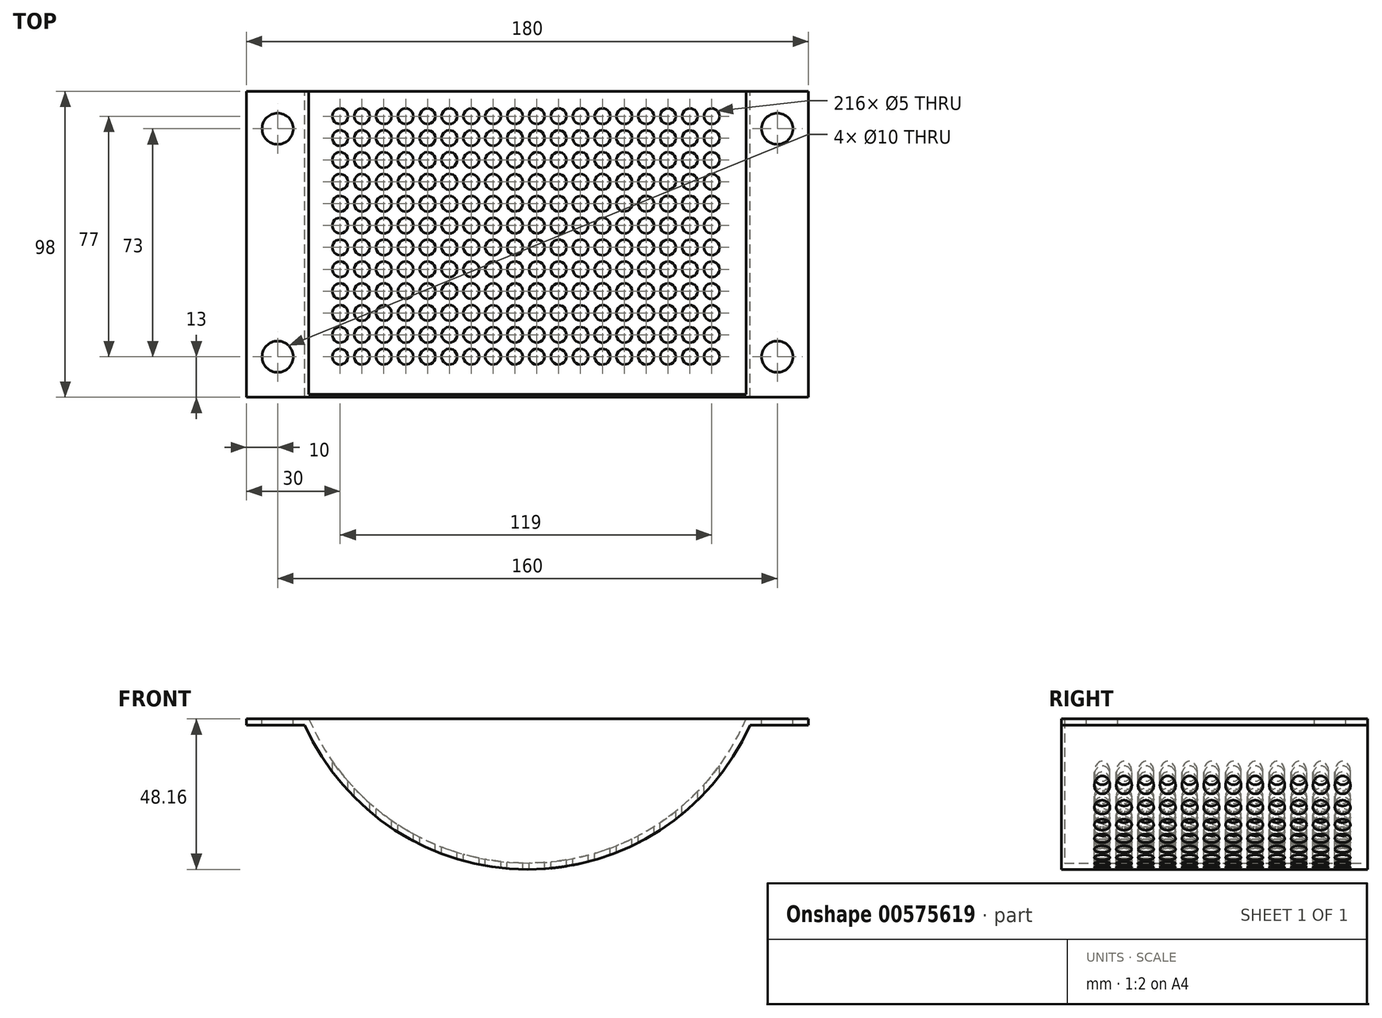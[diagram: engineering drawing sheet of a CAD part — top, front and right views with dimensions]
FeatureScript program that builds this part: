
annotation { "Feature Type Name" : "Feature", "Feature Type Description" : "" }
export const myFeature = defineFeature(function(context is Context, id is Id, definition is map)
    precondition{}
    {
        {
            var Q0;
            Q0=qCreatedBy(makeId("Front.planeOp"),FACE);
            var sketch = newSketch(context, id + "F0", { "sketchPlane" : qUnion([Q0])});
            skArc(sketch, "E0", {"start": v(-70, 0) * mm, "mid": v(-41.92, -33.58) * mm, "end": v(0, -46.16) * mm});
            skLineSegment(sketch, "E1", {"start": v(-70, 0) * mm, "end": v(-90, 0) * mm});
            skLineSegment(sketch, "E2", {"start": v(0, 0) * mm, "end": v(0, -46.16) * mm});
            skLineSegment(sketch, "E3.0", {"start": v(-71.3, -2) * mm, "end": v(-90, -2) * mm});
            skArc(sketch, "E3.1", {"start": v(-71.3, -2) * mm, "mid": v(-42.47, -35.61) * mm, "end": v(0, -48.16) * mm});
            skLineSegment(sketch, "E4", {"start": v(-90, 0) * mm, "end": v(-90, -2) * mm});
            skArc(sketch, "E5.MirrorCS", {"start": v(70, 0) * mm, "mid": v(41.92, -33.58) * mm, "end": v(0, -46.16) * mm});
            skArc(sketch, "E6.MirrorCS", {"start": v(71.3, -2) * mm, "mid": v(42.47, -35.61) * mm, "end": v(0, -48.16) * mm});
            skLineSegment(sketch, "E7.MirrorCS", {"start": v(71.3, -2) * mm, "end": v(90, -2) * mm});
            skLineSegment(sketch, "E8.MirrorCS", {"start": v(70, 0) * mm, "end": v(90, 0) * mm});
            skLineSegment(sketch, "E9.MirrorCS", {"start": v(90, 0) * mm, "end": v(90, -2) * mm});
            skSolve(sketch);
        }
        {
            var Q0;
            Q0 = qSketchRegion(id + "F0", true);
            extrude(context, id + "F1", {"entities" : qUnion([Q0]), "depth" : 97 * mm, "offsetDistance" : 25 * mm});
        }
        {
            var Q0;
            Q0=qCreatedBy(makeId("Top.planeOp"),FACE);
            var sketch = newSketch(context, id + "F2", { "sketchPlane" : qUnion([Q0])});
            skCircle(sketch, "E10", {"center": v(-60, -8) * mm, "radius": 2.5 * mm});
            skCircle(sketch, "E11.1.0.0", {"center": v(-53, -8) * mm, "radius": 2.5 * mm});
            skCircle(sketch, "E11.2.0.0", {"center": v(-46, -8) * mm, "radius": 2.5 * mm});
            skCircle(sketch, "E11.3.0.0", {"center": v(-39, -8) * mm, "radius": 2.5 * mm});
            skCircle(sketch, "E11.4.0.0", {"center": v(-32, -8) * mm, "radius": 2.5 * mm});
            skCircle(sketch, "E11.5.0.0", {"center": v(-25, -8) * mm, "radius": 2.5 * mm});
            skCircle(sketch, "E11.6.0.0", {"center": v(-18, -8) * mm, "radius": 2.5 * mm});
            skCircle(sketch, "E11.7.0.0", {"center": v(-11, -8) * mm, "radius": 2.5 * mm});
            skCircle(sketch, "E11.8.0.0", {"center": v(-4, -8) * mm, "radius": 2.5 * mm});
            skCircle(sketch, "E11.9.0.0", {"center": v(3, -8) * mm, "radius": 2.5 * mm});
            skCircle(sketch, "E11.10.0.0", {"center": v(10, -8) * mm, "radius": 2.5 * mm});
            skCircle(sketch, "E11.11.0.0", {"center": v(17, -8) * mm, "radius": 2.5 * mm});
            skCircle(sketch, "E11.12.0.0", {"center": v(24, -8) * mm, "radius": 2.5 * mm});
            skCircle(sketch, "E11.13.0.0", {"center": v(31, -8) * mm, "radius": 2.5 * mm});
            skCircle(sketch, "E11.14.0.0", {"center": v(38, -8) * mm, "radius": 2.5 * mm});
            skCircle(sketch, "E11.15.0.0", {"center": v(45, -8) * mm, "radius": 2.5 * mm});
            skCircle(sketch, "E11.16.0.0", {"center": v(52, -8) * mm, "radius": 2.5 * mm});
            skCircle(sketch, "E11.17.0.0", {"center": v(59, -8) * mm, "radius": 2.5 * mm});
            skLineSegment(sketch, "E11.direction1", {"start": v(-60, -8) * mm, "end": v(-53, -8) * mm, "construction": true});
            skCircle(sketch, "E12.1.0.0", {"center": v(-60, -15) * mm, "radius": 2.5 * mm});
            skCircle(sketch, "E12.1.0.1", {"center": v(-53, -15) * mm, "radius": 2.5 * mm});
            skCircle(sketch, "E12.1.0.2", {"center": v(-46, -15) * mm, "radius": 2.5 * mm});
            skCircle(sketch, "E12.1.0.3", {"center": v(-39, -15) * mm, "radius": 2.5 * mm});
            skCircle(sketch, "E12.1.0.4", {"center": v(-32, -15) * mm, "radius": 2.5 * mm});
            skCircle(sketch, "E12.1.0.5", {"center": v(-25, -15) * mm, "radius": 2.5 * mm});
            skCircle(sketch, "E12.1.0.6", {"center": v(-18, -15) * mm, "radius": 2.5 * mm});
            skCircle(sketch, "E12.1.0.7", {"center": v(-11, -15) * mm, "radius": 2.5 * mm});
            skCircle(sketch, "E12.1.0.8", {"center": v(-4, -15) * mm, "radius": 2.5 * mm});
            skCircle(sketch, "E12.1.0.9", {"center": v(3, -15) * mm, "radius": 2.5 * mm});
            skCircle(sketch, "E12.1.0.10", {"center": v(10, -15) * mm, "radius": 2.5 * mm});
            skCircle(sketch, "E12.1.0.11", {"center": v(17, -15) * mm, "radius": 2.5 * mm});
            skCircle(sketch, "E12.1.0.12", {"center": v(31, -15) * mm, "radius": 2.5 * mm});
            skCircle(sketch, "E12.1.0.13", {"center": v(38, -15) * mm, "radius": 2.5 * mm});
            skCircle(sketch, "E12.1.0.14", {"center": v(45, -15) * mm, "radius": 2.5 * mm});
            skCircle(sketch, "E12.1.0.15", {"center": v(52, -15) * mm, "radius": 2.5 * mm});
            skCircle(sketch, "E12.1.0.16", {"center": v(59, -15) * mm, "radius": 2.5 * mm});
            skCircle(sketch, "E12.2.0.0", {"center": v(-60, -22) * mm, "radius": 2.5 * mm});
            skCircle(sketch, "E12.2.0.1", {"center": v(-53, -22) * mm, "radius": 2.5 * mm});
            skCircle(sketch, "E12.2.0.2", {"center": v(-46, -22) * mm, "radius": 2.5 * mm});
            skCircle(sketch, "E12.2.0.3", {"center": v(-39, -22) * mm, "radius": 2.5 * mm});
            skCircle(sketch, "E12.2.0.4", {"center": v(-32, -22) * mm, "radius": 2.5 * mm});
            skCircle(sketch, "E12.2.0.5", {"center": v(-25, -22) * mm, "radius": 2.5 * mm});
            skCircle(sketch, "E12.2.0.6", {"center": v(-18, -22) * mm, "radius": 2.5 * mm});
            skCircle(sketch, "E12.2.0.7", {"center": v(-11, -22) * mm, "radius": 2.5 * mm});
            skCircle(sketch, "E12.2.0.8", {"center": v(-4, -22) * mm, "radius": 2.5 * mm});
            skCircle(sketch, "E12.2.0.9", {"center": v(3, -22) * mm, "radius": 2.5 * mm});
            skCircle(sketch, "E12.2.0.10", {"center": v(10, -22) * mm, "radius": 2.5 * mm});
            skCircle(sketch, "E12.2.0.11", {"center": v(17, -22) * mm, "radius": 2.5 * mm});
            skCircle(sketch, "E12.2.0.12", {"center": v(31, -22) * mm, "radius": 2.5 * mm});
            skCircle(sketch, "E12.2.0.13", {"center": v(38, -22) * mm, "radius": 2.5 * mm});
            skCircle(sketch, "E12.2.0.14", {"center": v(45, -22) * mm, "radius": 2.5 * mm});
            skCircle(sketch, "E12.2.0.15", {"center": v(52, -22) * mm, "radius": 2.5 * mm});
            skCircle(sketch, "E12.2.0.16", {"center": v(59, -22) * mm, "radius": 2.5 * mm});
            skCircle(sketch, "E12.3.0.0", {"center": v(-60, -29) * mm, "radius": 2.5 * mm});
            skCircle(sketch, "E12.3.0.1", {"center": v(-53, -29) * mm, "radius": 2.5 * mm});
            skCircle(sketch, "E12.3.0.2", {"center": v(-46, -29) * mm, "radius": 2.5 * mm});
            skCircle(sketch, "E12.3.0.3", {"center": v(-39, -29) * mm, "radius": 2.5 * mm});
            skCircle(sketch, "E12.3.0.4", {"center": v(-32, -29) * mm, "radius": 2.5 * mm});
            skCircle(sketch, "E12.3.0.5", {"center": v(-25, -29) * mm, "radius": 2.5 * mm});
            skCircle(sketch, "E12.3.0.6", {"center": v(-18, -29) * mm, "radius": 2.5 * mm});
            skCircle(sketch, "E12.3.0.7", {"center": v(-11, -29) * mm, "radius": 2.5 * mm});
            skCircle(sketch, "E12.3.0.8", {"center": v(-4, -29) * mm, "radius": 2.5 * mm});
            skCircle(sketch, "E12.3.0.9", {"center": v(3, -29) * mm, "radius": 2.5 * mm});
            skCircle(sketch, "E12.3.0.10", {"center": v(10, -29) * mm, "radius": 2.5 * mm});
            skCircle(sketch, "E12.3.0.11", {"center": v(17, -29) * mm, "radius": 2.5 * mm});
            skCircle(sketch, "E12.3.0.12", {"center": v(31, -29) * mm, "radius": 2.5 * mm});
            skCircle(sketch, "E12.3.0.13", {"center": v(38, -29) * mm, "radius": 2.5 * mm});
            skCircle(sketch, "E12.3.0.14", {"center": v(45, -29) * mm, "radius": 2.5 * mm});
            skCircle(sketch, "E12.3.0.15", {"center": v(52, -29) * mm, "radius": 2.5 * mm});
            skCircle(sketch, "E12.3.0.16", {"center": v(59, -29) * mm, "radius": 2.5 * mm});
            skCircle(sketch, "E12.4.0.0", {"center": v(-60, -36) * mm, "radius": 2.5 * mm});
            skCircle(sketch, "E12.4.0.1", {"center": v(-53, -36) * mm, "radius": 2.5 * mm});
            skCircle(sketch, "E12.4.0.2", {"center": v(-46, -36) * mm, "radius": 2.5 * mm});
            skCircle(sketch, "E12.4.0.3", {"center": v(-39, -36) * mm, "radius": 2.5 * mm});
            skCircle(sketch, "E12.4.0.4", {"center": v(-32, -36) * mm, "radius": 2.5 * mm});
            skCircle(sketch, "E12.4.0.5", {"center": v(-25, -36) * mm, "radius": 2.5 * mm});
            skCircle(sketch, "E12.4.0.6", {"center": v(-18, -36) * mm, "radius": 2.5 * mm});
            skCircle(sketch, "E12.4.0.7", {"center": v(-11, -36) * mm, "radius": 2.5 * mm});
            skCircle(sketch, "E12.4.0.8", {"center": v(-4, -36) * mm, "radius": 2.5 * mm});
            skCircle(sketch, "E12.4.0.9", {"center": v(3, -36) * mm, "radius": 2.5 * mm});
            skCircle(sketch, "E12.4.0.10", {"center": v(10, -36) * mm, "radius": 2.5 * mm});
            skCircle(sketch, "E12.4.0.11", {"center": v(17, -36) * mm, "radius": 2.5 * mm});
            skCircle(sketch, "E12.4.0.12", {"center": v(31, -36) * mm, "radius": 2.5 * mm});
            skCircle(sketch, "E12.4.0.13", {"center": v(38, -36) * mm, "radius": 2.5 * mm});
            skCircle(sketch, "E12.4.0.14", {"center": v(45, -36) * mm, "radius": 2.5 * mm});
            skCircle(sketch, "E12.4.0.15", {"center": v(52, -36) * mm, "radius": 2.5 * mm});
            skCircle(sketch, "E12.4.0.16", {"center": v(59, -36) * mm, "radius": 2.5 * mm});
            skCircle(sketch, "E12.5.0.0", {"center": v(-60, -43) * mm, "radius": 2.5 * mm});
            skCircle(sketch, "E12.5.0.1", {"center": v(-53, -43) * mm, "radius": 2.5 * mm});
            skCircle(sketch, "E12.5.0.2", {"center": v(-46, -43) * mm, "radius": 2.5 * mm});
            skCircle(sketch, "E12.5.0.3", {"center": v(-39, -43) * mm, "radius": 2.5 * mm});
            skCircle(sketch, "E12.5.0.4", {"center": v(-32, -43) * mm, "radius": 2.5 * mm});
            skCircle(sketch, "E12.5.0.5", {"center": v(-25, -43) * mm, "radius": 2.5 * mm});
            skCircle(sketch, "E12.5.0.6", {"center": v(-18, -43) * mm, "radius": 2.5 * mm});
            skCircle(sketch, "E12.5.0.7", {"center": v(-11, -43) * mm, "radius": 2.5 * mm});
            skCircle(sketch, "E12.5.0.8", {"center": v(-4, -43) * mm, "radius": 2.5 * mm});
            skCircle(sketch, "E12.5.0.9", {"center": v(3, -43) * mm, "radius": 2.5 * mm});
            skCircle(sketch, "E12.5.0.10", {"center": v(10, -43) * mm, "radius": 2.5 * mm});
            skCircle(sketch, "E12.5.0.11", {"center": v(17, -43) * mm, "radius": 2.5 * mm});
            skCircle(sketch, "E12.5.0.12", {"center": v(31, -43) * mm, "radius": 2.5 * mm});
            skCircle(sketch, "E12.5.0.13", {"center": v(38, -43) * mm, "radius": 2.5 * mm});
            skCircle(sketch, "E12.5.0.14", {"center": v(45, -43) * mm, "radius": 2.5 * mm});
            skCircle(sketch, "E12.5.0.15", {"center": v(52, -43) * mm, "radius": 2.5 * mm});
            skCircle(sketch, "E12.5.0.16", {"center": v(59, -43) * mm, "radius": 2.5 * mm});
            skCircle(sketch, "E12.6.0.0", {"center": v(-60, -50) * mm, "radius": 2.5 * mm});
            skCircle(sketch, "E12.6.0.1", {"center": v(-53, -50) * mm, "radius": 2.5 * mm});
            skCircle(sketch, "E12.6.0.2", {"center": v(-46, -50) * mm, "radius": 2.5 * mm});
            skCircle(sketch, "E12.6.0.3", {"center": v(-39, -50) * mm, "radius": 2.5 * mm});
            skCircle(sketch, "E12.6.0.4", {"center": v(-32, -50) * mm, "radius": 2.5 * mm});
            skCircle(sketch, "E12.6.0.5", {"center": v(-25, -50) * mm, "radius": 2.5 * mm});
            skCircle(sketch, "E12.6.0.6", {"center": v(-18, -50) * mm, "radius": 2.5 * mm});
            skCircle(sketch, "E12.6.0.7", {"center": v(-11, -50) * mm, "radius": 2.5 * mm});
            skCircle(sketch, "E12.6.0.8", {"center": v(-4, -50) * mm, "radius": 2.5 * mm});
            skCircle(sketch, "E12.6.0.9", {"center": v(3, -50) * mm, "radius": 2.5 * mm});
            skCircle(sketch, "E12.6.0.10", {"center": v(10, -50) * mm, "radius": 2.5 * mm});
            skCircle(sketch, "E12.6.0.11", {"center": v(17, -50) * mm, "radius": 2.5 * mm});
            skCircle(sketch, "E12.6.0.12", {"center": v(31, -50) * mm, "radius": 2.5 * mm});
            skCircle(sketch, "E12.6.0.13", {"center": v(38, -50) * mm, "radius": 2.5 * mm});
            skCircle(sketch, "E12.6.0.14", {"center": v(45, -50) * mm, "radius": 2.5 * mm});
            skCircle(sketch, "E12.6.0.15", {"center": v(52, -50) * mm, "radius": 2.5 * mm});
            skCircle(sketch, "E12.6.0.16", {"center": v(59, -50) * mm, "radius": 2.5 * mm});
            skCircle(sketch, "E12.7.0.0", {"center": v(-60, -57) * mm, "radius": 2.5 * mm});
            skCircle(sketch, "E12.7.0.1", {"center": v(-53, -57) * mm, "radius": 2.5 * mm});
            skCircle(sketch, "E12.7.0.2", {"center": v(-46, -57) * mm, "radius": 2.5 * mm});
            skCircle(sketch, "E12.7.0.3", {"center": v(-39, -57) * mm, "radius": 2.5 * mm});
            skCircle(sketch, "E12.7.0.4", {"center": v(-32, -57) * mm, "radius": 2.5 * mm});
            skCircle(sketch, "E12.7.0.5", {"center": v(-25, -57) * mm, "radius": 2.5 * mm});
            skCircle(sketch, "E12.7.0.6", {"center": v(-18, -57) * mm, "radius": 2.5 * mm});
            skCircle(sketch, "E12.7.0.7", {"center": v(-11, -57) * mm, "radius": 2.5 * mm});
            skCircle(sketch, "E12.7.0.8", {"center": v(-4, -57) * mm, "radius": 2.5 * mm});
            skCircle(sketch, "E12.7.0.9", {"center": v(3, -57) * mm, "radius": 2.5 * mm});
            skCircle(sketch, "E12.7.0.10", {"center": v(10, -57) * mm, "radius": 2.5 * mm});
            skCircle(sketch, "E12.7.0.11", {"center": v(17, -57) * mm, "radius": 2.5 * mm});
            skCircle(sketch, "E12.7.0.12", {"center": v(31, -57) * mm, "radius": 2.5 * mm});
            skCircle(sketch, "E12.7.0.13", {"center": v(38, -57) * mm, "radius": 2.5 * mm});
            skCircle(sketch, "E12.7.0.14", {"center": v(45, -57) * mm, "radius": 2.5 * mm});
            skCircle(sketch, "E12.7.0.15", {"center": v(52, -57) * mm, "radius": 2.5 * mm});
            skCircle(sketch, "E12.7.0.16", {"center": v(59, -57) * mm, "radius": 2.5 * mm});
            skCircle(sketch, "E12.8.0.0", {"center": v(-60, -64) * mm, "radius": 2.5 * mm});
            skCircle(sketch, "E12.8.0.1", {"center": v(-53, -64) * mm, "radius": 2.5 * mm});
            skCircle(sketch, "E12.8.0.2", {"center": v(-46, -64) * mm, "radius": 2.5 * mm});
            skCircle(sketch, "E12.8.0.3", {"center": v(-39, -64) * mm, "radius": 2.5 * mm});
            skCircle(sketch, "E12.8.0.4", {"center": v(-32, -64) * mm, "radius": 2.5 * mm});
            skCircle(sketch, "E12.8.0.5", {"center": v(-25, -64) * mm, "radius": 2.5 * mm});
            skCircle(sketch, "E12.8.0.6", {"center": v(-18, -64) * mm, "radius": 2.5 * mm});
            skCircle(sketch, "E12.8.0.7", {"center": v(-11, -64) * mm, "radius": 2.5 * mm});
            skCircle(sketch, "E12.8.0.8", {"center": v(-4, -64) * mm, "radius": 2.5 * mm});
            skCircle(sketch, "E12.8.0.9", {"center": v(3, -64) * mm, "radius": 2.5 * mm});
            skCircle(sketch, "E12.8.0.10", {"center": v(10, -64) * mm, "radius": 2.5 * mm});
            skCircle(sketch, "E12.8.0.11", {"center": v(17, -64) * mm, "radius": 2.5 * mm});
            skCircle(sketch, "E12.8.0.12", {"center": v(31, -64) * mm, "radius": 2.5 * mm});
            skCircle(sketch, "E12.8.0.13", {"center": v(38, -64) * mm, "radius": 2.5 * mm});
            skCircle(sketch, "E12.8.0.14", {"center": v(45, -64) * mm, "radius": 2.5 * mm});
            skCircle(sketch, "E12.8.0.15", {"center": v(52, -64) * mm, "radius": 2.5 * mm});
            skCircle(sketch, "E12.8.0.16", {"center": v(59, -64) * mm, "radius": 2.5 * mm});
            skCircle(sketch, "E12.9.0.0", {"center": v(-60, -71) * mm, "radius": 2.5 * mm});
            skCircle(sketch, "E12.9.0.1", {"center": v(-53, -71) * mm, "radius": 2.5 * mm});
            skCircle(sketch, "E12.9.0.2", {"center": v(-46, -71) * mm, "radius": 2.5 * mm});
            skCircle(sketch, "E12.9.0.3", {"center": v(-39, -71) * mm, "radius": 2.5 * mm});
            skCircle(sketch, "E12.9.0.4", {"center": v(-32, -71) * mm, "radius": 2.5 * mm});
            skCircle(sketch, "E12.9.0.5", {"center": v(-25, -71) * mm, "radius": 2.5 * mm});
            skCircle(sketch, "E12.9.0.6", {"center": v(-18, -71) * mm, "radius": 2.5 * mm});
            skCircle(sketch, "E12.9.0.7", {"center": v(-11, -71) * mm, "radius": 2.5 * mm});
            skCircle(sketch, "E12.9.0.8", {"center": v(-4, -71) * mm, "radius": 2.5 * mm});
            skCircle(sketch, "E12.9.0.9", {"center": v(3, -71) * mm, "radius": 2.5 * mm});
            skCircle(sketch, "E12.9.0.10", {"center": v(10, -71) * mm, "radius": 2.5 * mm});
            skCircle(sketch, "E12.9.0.11", {"center": v(17, -71) * mm, "radius": 2.5 * mm});
            skCircle(sketch, "E12.9.0.12", {"center": v(31, -71) * mm, "radius": 2.5 * mm});
            skCircle(sketch, "E12.9.0.13", {"center": v(38, -71) * mm, "radius": 2.5 * mm});
            skCircle(sketch, "E12.9.0.14", {"center": v(45, -71) * mm, "radius": 2.5 * mm});
            skCircle(sketch, "E12.9.0.15", {"center": v(52, -71) * mm, "radius": 2.5 * mm});
            skCircle(sketch, "E12.9.0.16", {"center": v(59, -71) * mm, "radius": 2.5 * mm});
            skCircle(sketch, "E12.10.0.0", {"center": v(-60, -78) * mm, "radius": 2.5 * mm});
            skCircle(sketch, "E12.10.0.1", {"center": v(-53, -78) * mm, "radius": 2.5 * mm});
            skCircle(sketch, "E12.10.0.2", {"center": v(-46, -78) * mm, "radius": 2.5 * mm});
            skCircle(sketch, "E12.10.0.3", {"center": v(-39, -78) * mm, "radius": 2.5 * mm});
            skCircle(sketch, "E12.10.0.4", {"center": v(-32, -78) * mm, "radius": 2.5 * mm});
            skCircle(sketch, "E12.10.0.5", {"center": v(-25, -78) * mm, "radius": 2.5 * mm});
            skCircle(sketch, "E12.10.0.6", {"center": v(-18, -78) * mm, "radius": 2.5 * mm});
            skCircle(sketch, "E12.10.0.7", {"center": v(-11, -78) * mm, "radius": 2.5 * mm});
            skCircle(sketch, "E12.10.0.8", {"center": v(-4, -78) * mm, "radius": 2.5 * mm});
            skCircle(sketch, "E12.10.0.9", {"center": v(3, -78) * mm, "radius": 2.5 * mm});
            skCircle(sketch, "E12.10.0.10", {"center": v(10, -78) * mm, "radius": 2.5 * mm});
            skCircle(sketch, "E12.10.0.11", {"center": v(17, -78) * mm, "radius": 2.5 * mm});
            skCircle(sketch, "E12.10.0.12", {"center": v(31, -78) * mm, "radius": 2.5 * mm});
            skCircle(sketch, "E12.10.0.13", {"center": v(38, -78) * mm, "radius": 2.5 * mm});
            skCircle(sketch, "E12.10.0.14", {"center": v(45, -78) * mm, "radius": 2.5 * mm});
            skCircle(sketch, "E12.10.0.15", {"center": v(52, -78) * mm, "radius": 2.5 * mm});
            skCircle(sketch, "E12.10.0.16", {"center": v(59, -78) * mm, "radius": 2.5 * mm});
            skCircle(sketch, "E12.11.0.0", {"center": v(-60, -85) * mm, "radius": 2.5 * mm});
            skCircle(sketch, "E12.11.0.1", {"center": v(-53, -85) * mm, "radius": 2.5 * mm});
            skCircle(sketch, "E12.11.0.2", {"center": v(-46, -85) * mm, "radius": 2.5 * mm});
            skCircle(sketch, "E12.11.0.3", {"center": v(-39, -85) * mm, "radius": 2.5 * mm});
            skCircle(sketch, "E12.11.0.4", {"center": v(-32, -85) * mm, "radius": 2.5 * mm});
            skCircle(sketch, "E12.11.0.5", {"center": v(-25, -85) * mm, "radius": 2.5 * mm});
            skCircle(sketch, "E12.11.0.6", {"center": v(-18, -85) * mm, "radius": 2.5 * mm});
            skCircle(sketch, "E12.11.0.7", {"center": v(-11, -85) * mm, "radius": 2.5 * mm});
            skCircle(sketch, "E12.11.0.8", {"center": v(-4, -85) * mm, "radius": 2.5 * mm});
            skCircle(sketch, "E12.11.0.9", {"center": v(3, -85) * mm, "radius": 2.5 * mm});
            skCircle(sketch, "E12.11.0.10", {"center": v(10, -85) * mm, "radius": 2.5 * mm});
            skCircle(sketch, "E12.11.0.11", {"center": v(17, -85) * mm, "radius": 2.5 * mm});
            skCircle(sketch, "E12.11.0.12", {"center": v(31, -85) * mm, "radius": 2.5 * mm});
            skCircle(sketch, "E12.11.0.13", {"center": v(38, -85) * mm, "radius": 2.5 * mm});
            skCircle(sketch, "E12.11.0.14", {"center": v(45, -85) * mm, "radius": 2.5 * mm});
            skCircle(sketch, "E12.11.0.15", {"center": v(52, -85) * mm, "radius": 2.5 * mm});
            skCircle(sketch, "E12.11.0.16", {"center": v(59, -85) * mm, "radius": 2.5 * mm});
            skLineSegment(sketch, "E12.direction1", {"start": v(-60, -8) * mm, "end": v(-60, -15) * mm, "construction": true});
            skCircle(sketch, "E13.1.0.0", {"center": v(24, -15) * mm, "radius": 2.5 * mm});
            skCircle(sketch, "E13.2.0.0", {"center": v(24, -22) * mm, "radius": 2.5 * mm});
            skCircle(sketch, "E13.3.0.0", {"center": v(24, -29) * mm, "radius": 2.5 * mm});
            skCircle(sketch, "E13.4.0.0", {"center": v(24, -36) * mm, "radius": 2.5 * mm});
            skCircle(sketch, "E13.5.0.0", {"center": v(24, -43) * mm, "radius": 2.5 * mm});
            skCircle(sketch, "E13.6.0.0", {"center": v(24, -50) * mm, "radius": 2.5 * mm});
            skCircle(sketch, "E13.7.0.0", {"center": v(24, -57) * mm, "radius": 2.5 * mm});
            skCircle(sketch, "E13.8.0.0", {"center": v(24, -64) * mm, "radius": 2.5 * mm});
            skCircle(sketch, "E13.9.0.0", {"center": v(24, -71) * mm, "radius": 2.5 * mm});
            skCircle(sketch, "E13.10.0.0", {"center": v(24, -78) * mm, "radius": 2.5 * mm});
            skCircle(sketch, "E13.11.0.0", {"center": v(24, -85) * mm, "radius": 2.5 * mm});
            skLineSegment(sketch, "E13.direction1", {"start": v(24, -8) * mm, "end": v(24, -15) * mm, "construction": true});
            skSolve(sketch);
        }
        {
            var Q0;
            Q0 = qSketchRegion(id + "F2", true);
            extrude(context, id + "F3", {"entities" : qUnion([Q0]), "operationType" : NewBodyOperationType.REMOVE, "endBound" : BoundingType.THROUGH_ALL, "oppositeDirection" : true, "depth" : 25 * mm, "offsetDistance" : 25 * mm});
        }
        {
            var Q0;
            Q0=qCreatedBy(makeId("Top.planeOp"),FACE);
            var sketch = newSketch(context, id + "F4", { "sketchPlane" : qUnion([Q0])});
            skCircle(sketch, "E14", {"center": v(-80, -12) * mm, "radius": 5 * mm});
            skCircle(sketch, "E15.MirrorC", {"center": v(80, -12) * mm, "radius": 5 * mm});
            skLineSegment(sketch, "E16", {"start": v(90.51, -48.5) * mm, "end": v(-112.77, -48.5) * mm});
            skLineSegment(sketch, "E17", {"start": v(0, 0) * mm, "end": v(0, -97) * mm});
            skCircle(sketch, "E18.MirrorC", {"center": v(-80, -85) * mm, "radius": 5 * mm});
            skCircle(sketch, "E19.MirrorC", {"center": v(80, -85) * mm, "radius": 5 * mm});
            skSolve(sketch);
        }
        {
            var Q0;
            Q0 = qSketchRegion(id + "F4", true);
            extrude(context, id + "F5", {"entities" : qUnion([Q0]), "operationType" : NewBodyOperationType.REMOVE, "oppositeDirection" : true, "depth" : 25 * mm, "offsetDistance" : 25 * mm});
        }
        {
            var Q0;
            Q0=makeQuery(id+"F1.opExtrude","CAP_FACE",FACE,{"disambiguationData":[OSD([sQuery(id+"F0.wireOp",EDGE,"E0"),sQuery(id+"F0.wireOp",EDGE,"E1"),sQuery(id+"F0.wireOp",EDGE,"E3.0"),sQuery(id+"F0.wireOp",EDGE,"E3.1"),sQuery(id+"F0.wireOp",EDGE,"E4"),sQuery(id+"F0.wireOp",EDGE,"E5.MirrorCS"),sQuery(id+"F0.wireOp",EDGE,"E6.MirrorCS"),sQuery(id+"F0.wireOp",EDGE,"E7.MirrorCS"),sQuery(id+"F0.wireOp",EDGE,"E8.MirrorCS"),sQuery(id+"F0.wireOp",EDGE,"E9.MirrorCS")])],"isStart":false});
            var sketch = newSketch(context, id + "F6", { "sketchPlane" : qUnion([Q0])});
            skLineSegment(sketch, "E20.0.0", {"start": v(90, 0) * mm, "end": v(70, 0) * mm});
            skLineSegment(sketch, "E20.0.2", {"start": v(-70, 0) * mm, "end": v(-90, 0) * mm});
            skLineSegment(sketch, "E20.0.3", {"start": v(-90, 0) * mm, "end": v(-90, -2) * mm});
            skLineSegment(sketch, "E20.0.4", {"start": v(-90, -2) * mm, "end": v(-71.3, -2) * mm});
            skArc(sketch, "E20.0.5", {"start": v(-71.3, -2) * mm, "mid": v(0, -48.16) * mm, "end": v(71.3, -2) * mm});
            skLineSegment(sketch, "E20.0.6", {"start": v(71.3, -2) * mm, "end": v(90, -2) * mm});
            skLineSegment(sketch, "E20.0.7", {"start": v(90, -2) * mm, "end": v(90, 0) * mm});
            skLineSegment(sketch, "E21", {"start": v(-70, 0) * mm, "end": v(70, 0) * mm});
            skSolve(sketch);
        }
        {
            var Q0;
            Q0 = qSketchRegion(id + "F6", true);
            extrude(context, id + "F7", {"entities" : qUnion([Q0]), "operationType" : NewBodyOperationType.ADD, "depth" : 1 * mm, "offsetDistance" : 25 * mm});
        }
    });
